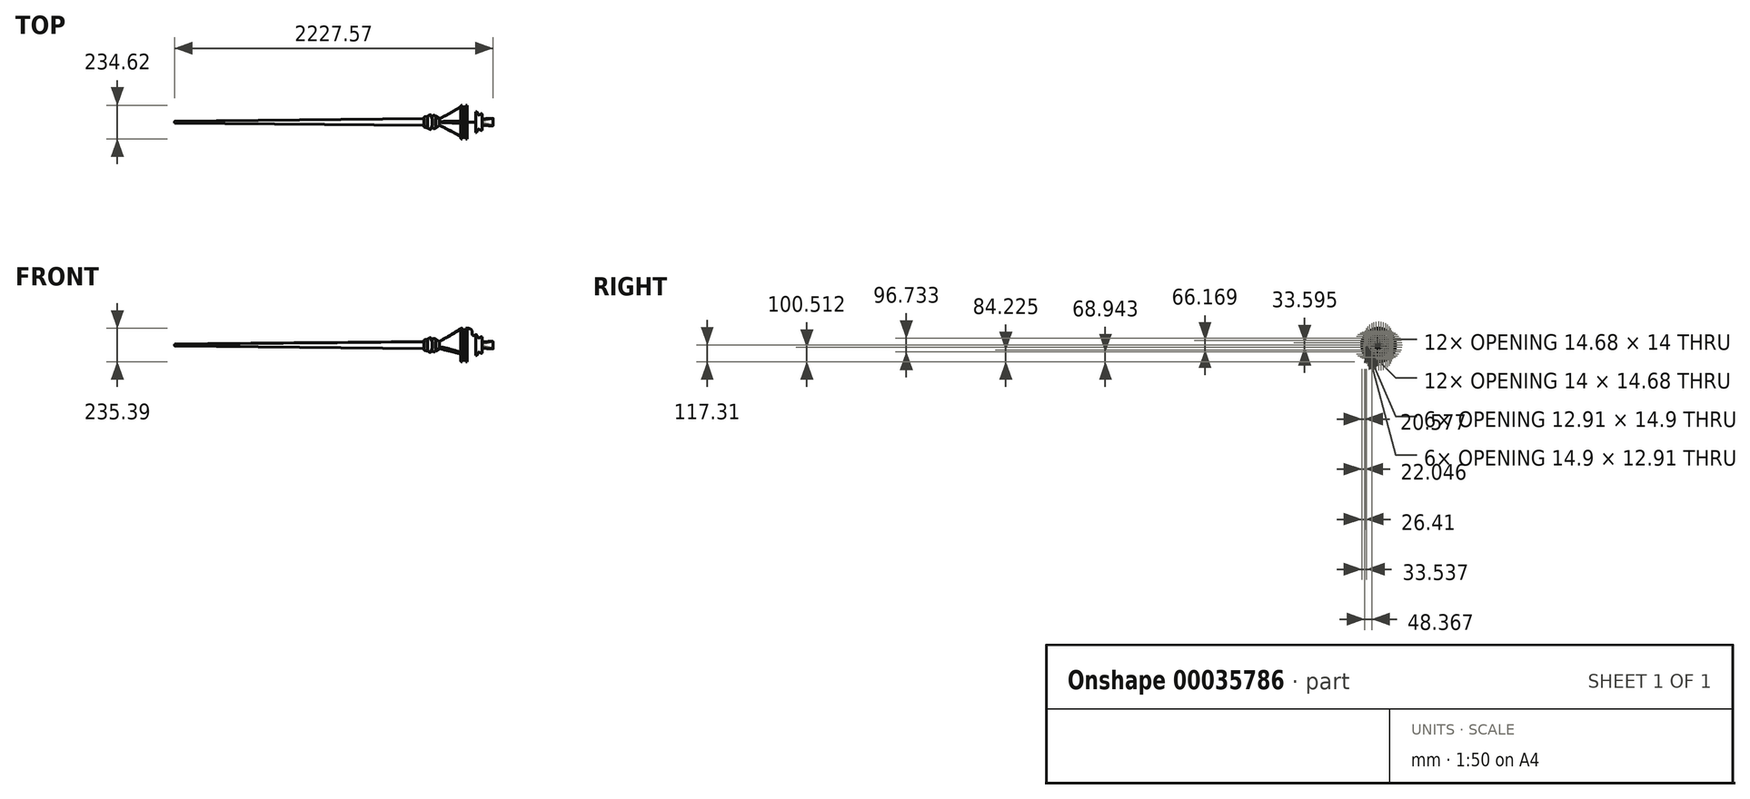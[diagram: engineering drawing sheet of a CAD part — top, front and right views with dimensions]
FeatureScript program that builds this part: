
annotation { "Feature Type Name" : "Feature", "Feature Type Description" : "" }
export const myFeature = defineFeature(function(context is Context, id is Id, definition is map)
    precondition{}
    {
        {
            var Q0;
            Q0=qCreatedBy(makeId("Front.planeOp"),FACE);
            var sketch = newSketch(context, id + "F0", { "sketchPlane" : qUnion([Q0])});
            skLineSegment(sketch, "E0.top", {"start": v(-36.48, 0) * mm, "end": v(43.13, 0) * mm});
            skLineSegment(sketch, "E0.left", {"start": v(-36.48, 5.03) * mm, "end": v(-36.48, 0) * mm});
            skLineSegment(sketch, "E0.right", {"start": v(43.13, 21.56) * mm, "end": v(43.13, 0) * mm});
            skLineSegment(sketch, "E1", {"start": v(-36.48, 5.03) * mm, "end": v(-68.97, 32.77) * mm});
            skLineSegment(sketch, "E2", {"start": v(-68.97, 32.77) * mm, "end": v(-38.76, 38.47) * mm});
            skLineSegment(sketch, "E3", {"start": v(-38.76, 38.47) * mm, "end": v(-17.29, 51.96) * mm});
            skLineSegment(sketch, "E4", {"start": v(-17.29, 51.96) * mm, "end": v(-14.44, 24.41) * mm});
            skLineSegment(sketch, "E5", {"start": v(-14.44, 24.41) * mm, "end": v(-1.7, 21.56) * mm});
            skArc(sketch, "E6", {"start": v(15, 39.61) * mm, "mid": v(-3.59, 40.07) * mm, "end": v(-1.7, 21.56) * mm});
            skLineSegment(sketch, "E7", {"start": v(15, 39.61) * mm, "end": v(43.13, 21.56) * mm});
            skSolve(sketch);
        }
        {
            var Q0;
            Q0=makeQuery(id+"F0.imprint","IMPRINT",FACE,{"disambiguationData":[TD([[makeQuery(id+"F0.imprint","IMPRINT",EDGE,{"derivedFrom":sQuery(id+"F0.wireOp",EDGE,"E0.top")}),1.0]])]});
            var Q1;
            Q1=sQuery(id+"F0.wireOp",EDGE,"E0.top");
            var Q2;
            Q2=sQuery(id+"F0.wireOp",EDGE,"E0.top");
            revolve(context, id + "F1", {"entities" : qUnion([Q0]), "surfaceEntities" : qUnion([Q1]), "axis" : qUnion([Q2]), "revolveType" : RevolveType.FULL});
        }
        {
            var Q0;
            Q0=makeQuery(id+"F1.opRevolve","SWEPT_FACE",FACE,{"disambiguationData":[OSD([sQuery(id+"F0.wireOp",EDGE,"E0.right")])]});
            cPlane(context, id + "F2", {"entities" : qUnion([Q0]), "cplaneType" : CPlaneType.OFFSET, "offset" : 150 * mm, "width" : 150 * mm, "height" : 150 * mm});
        }
        {
            var Q0;
            Q0=qCreatedBy(id+"F2.planeOp",FACE);
            var sketch = newSketch(context, id + "F3", { "sketchPlane" : qUnion([Q0])});
            skCircle(sketch, "E8.cCircle", {"center": v(0, 0) * mm, "radius": 58.56 * mm, "construction": true});
            skLineSegment(sketch, "E8.0", {"start": v(-101.43, -58.56) * mm, "end": v(0, 117.12) * mm});
            skLineSegment(sketch, "E8.1", {"start": v(0, 117.12) * mm, "end": v(101.43, -58.56) * mm});
            skLineSegment(sketch, "E8.2", {"start": v(101.43, -58.56) * mm, "end": v(-101.43, -58.56) * mm});
            skPoint(sketch, "E8.0.midPoint", {"position": v(-50.71, 29.28) * mm});
            skLineSegment(sketch, "E9", {"start": v(0, 0) * mm, "end": v(0, 152.92) * mm, "construction": true});
            skSolve(sketch);
        }
        {
            var Q1;
            Q1=makeQuery(id+"F1.opRevolve","SWEPT_FACE",FACE,{"disambiguationData":[OSD([sQuery(id+"F0.wireOp",EDGE,"E0.right")])]});
            var Q2;
            Q2=makeQuery(id+"F3.imprint","IMPRINT",FACE,{"disambiguationData":[TD([[makeQuery(id+"F3.imprint","IMPRINT",EDGE,{"derivedFrom":sQuery(id+"F3.wireOp",EDGE,"E8.0")}),-1.0]])]});
            loft(context, id + "F4", {"operationType" : NewBodyOperationType.ADD, "sheetProfilesArray" : [{ "sheetProfileEntities" : qUnion([Q1]) }, { "sheetProfileEntities" : qUnion([Q2]) }]});
        }
        {
            var Q0;
            {var subQ0=sQuery(id+"F3.wireOp",EDGE,"E8.2");var subQ1=sQuery(id+"F3.wireOp",EDGE,"E8.1");var subQ2=sQuery(id+"F3.wireOp",EDGE,"E8.0");var subQ3=sQuery(id+"F0.wireOp",EDGE,"E7");var subQ4=sQuery(id+"F0.wireOp",EDGE,"E0.right");Q0=makeQuery(id+"F4.opLoft","SWEPT_EDGE",EDGE,{"disambiguationData":[OSD([subQ4,subQ3,subQ2,subQ1,subQ0]),TDD([makeQuery(id+"F1.opRevolve","SWEPT_EDGE",EDGE,{"disambiguationData":[OSD([subQ4,subQ3])]}),makeQuery(id+"F3.imprint","INTERSECT",VERTEX,{"derivedFrom":[subQ2,subQ1]}),makeQuery(id+"F3.imprint","INTERSECT",VERTEX,{"derivedFrom":[subQ1,subQ0]})])]});}
            var Q1;
            {var subQ0=sQuery(id+"F3.wireOp",EDGE,"E8.2");var subQ1=sQuery(id+"F3.wireOp",EDGE,"E8.1");var subQ2=sQuery(id+"F3.wireOp",EDGE,"E8.0");var subQ3=sQuery(id+"F0.wireOp",EDGE,"E7");var subQ4=sQuery(id+"F0.wireOp",EDGE,"E0.right");Q1=makeQuery(id+"F4.opLoft","SWEPT_EDGE",EDGE,{"disambiguationData":[OSD([subQ4,subQ3,subQ2,subQ1,subQ0]),TDD([makeQuery(id+"F1.opRevolve","SWEPT_EDGE",EDGE,{"disambiguationData":[OSD([subQ4,subQ3])]}),makeQuery(id+"F3.imprint","INTERSECT",VERTEX,{"derivedFrom":[subQ2,subQ0]}),makeQuery(id+"F3.imprint","INTERSECT",VERTEX,{"derivedFrom":[subQ1,subQ0]})])]});}
            var Q2;
            Q2=makeQuery(id+"F4.opLoft","SWEPT_EDGE",EDGE,{"disambiguationData":[OSD([sQuery(id+"F3.wireOp",EDGE,"E8.0"),sQuery(id+"F3.wireOp",EDGE,"E8.2")])]});
            var Q3;
            Q3=makeQuery(id+"F1.opRevolve","SWEPT_EDGE",EDGE,{"disambiguationData":[OSD([sQuery(id+"F0.wireOp",EDGE,"E1"),sQuery(id+"F0.wireOp",EDGE,"E2")])]});
            var Q4;
            Q4=makeQuery(id+"F1.opRevolve","SWEPT_EDGE",EDGE,{"disambiguationData":[OSD([sQuery(id+"F0.wireOp",EDGE,"E3"),sQuery(id+"F0.wireOp",EDGE,"E4")])]});
            var Q5;
            Q5=makeQuery(id+"F1.opRevolve","SWEPT_EDGE",EDGE,{"disambiguationData":[OSD([sQuery(id+"F0.wireOp",EDGE,"E4"),sQuery(id+"F0.wireOp",EDGE,"E5")])]});
            fillet(context, id + "F5", {"entities" : qUnion([Q0, Q1, Q2, Q3, Q4, Q5]), "radius" : 5 * mm, "tangentPropagation" : true, "allowEdgeOverflow" : false});
        }
        {
            var Q0;
            Q0=makeQuery(id+"F4.opLoft","CAP_FACE",FACE,{"disambiguationData":[OSD([makeQuery(id+"F3.imprint","IMPRINT",FACE,{"disambiguationData":[TD([[makeQuery(id+"F3.imprint","IMPRINT",EDGE,{"derivedFrom":sQuery(id+"F3.wireOp",EDGE,"E8.0")}),-1.0]])]})])],"isStart":true});
            cPlane(context, id + "F6", {"entities" : qUnion([Q0]), "cplaneType" : CPlaneType.OFFSET, "offset" : 50 * mm, "width" : 150 * mm, "height" : 150 * mm});
        }
        {
            var Q0;
            Q0=makeQuery(id+"F4.opLoft","CAP_FACE",FACE,{"disambiguationData":[OSD([makeQuery(id+"F3.imprint","IMPRINT",FACE,{"disambiguationData":[TD([[makeQuery(id+"F3.imprint","IMPRINT",EDGE,{"derivedFrom":sQuery(id+"F3.wireOp",EDGE,"E8.0")}),-1.0]])]})])],"isStart":true});
            var Q1;
            Q1=makeQuery(id+"F1.opRevolve","SWEPT_BODY",BODY,{"disambiguationData":[OSD([sQuery(id+"F0.wireOp",EDGE,"E0.top"),sQuery(id+"F0.wireOp",EDGE,"E0.left"),sQuery(id+"F0.wireOp",EDGE,"E0.right"),sQuery(id+"F0.wireOp",EDGE,"E1"),sQuery(id+"F0.wireOp",EDGE,"E2"),sQuery(id+"F0.wireOp",EDGE,"E3"),sQuery(id+"F0.wireOp",EDGE,"E4"),sQuery(id+"F0.wireOp",EDGE,"E5"),sQuery(id+"F0.wireOp",EDGE,"E6"),sQuery(id+"F0.wireOp",EDGE,"E7")])]});
            shell(context, id + "F7", {"entities" : qUnion([Q0]), "parts" : qUnion([Q1]), "thickness" : 2.5 * mm, "oppositeDirection" : true});
        }
        {
            var Q0;
            Q0=makeQuery(id+"F4.opLoft","CAP_FACE",FACE,{"disambiguationData":[OSD([makeQuery(id+"F3.imprint","IMPRINT",FACE,{"disambiguationData":[TD([[makeQuery(id+"F3.imprint","IMPRINT",EDGE,{"derivedFrom":sQuery(id+"F3.wireOp",EDGE,"E8.0")}),-1.0]])]})])],"isStart":true});
            var sketch = newSketch(context, id + "F8", { "sketchPlane" : qUnion([Q0])});
            skCircle(sketch, "E10", {"center": v(0, 0) * mm, "radius": 117.31 * mm});
            skSolve(sketch);
        }
        {
            var Q0;
            Q0 = qSketchRegion(id + "F8", true);
            extrude(context, id + "F9", {"entities" : qUnion([Q0]), "operationType" : NewBodyOperationType.ADD, "depth" : 10 * mm});
        }
        {
            var Q0;
            Q0=makeQuery(id+"F9.opExtrude","CAP_EDGE",EDGE,{"disambiguationData":[OSD([sQuery(id+"F8.wireOp",EDGE,"E10")])],"isStart":true});
            fillet(context, id + "F10", {"entities" : qUnion([Q0]), "radius" : 5 * mm, "tangentPropagation" : true, "allowEdgeOverflow" : false});
        }
        {
            var Q0;
            Q0=makeQuery(id+"F9.opExtrude","CAP_FACE",FACE,{"disambiguationData":[OSD([sQuery(id+"F8.wireOp",EDGE,"E10")])],"isStart":false});
            var sketch = newSketch(context, id + "F11", { "sketchPlane" : qUnion([Q0])});
            skCircle(sketch, "E11.cCircle", {"center": v(96.73, 0) * mm, "radius": 6.45 * mm, "construction": true});
            skLineSegment(sketch, "E11.0", {"start": v(93, 6.45) * mm, "end": v(100.46, 6.45) * mm});
            skLineSegment(sketch, "E11.1", {"start": v(100.46, 6.45) * mm, "end": v(104.19, 0) * mm});
            skLineSegment(sketch, "E11.2", {"start": v(104.19, 0) * mm, "end": v(100.46, -6.45) * mm});
            skLineSegment(sketch, "E11.3", {"start": v(100.46, -6.45) * mm, "end": v(93, -6.45) * mm});
            skLineSegment(sketch, "E11.4", {"start": v(93, -6.45) * mm, "end": v(89.28, 0) * mm});
            skLineSegment(sketch, "E11.5", {"start": v(89.28, 0) * mm, "end": v(93, 6.45) * mm});
            skPoint(sketch, "E11.0.midPoint", {"position": v(96.73, 6.45) * mm});
            skSolve(sketch);
        }
        {
            var Q0;
            Q0 = qSketchRegion(id + "F11", true);
            extrude(context, id + "F12", {"entities" : qUnion([Q0]), "depth" : 25 * mm});
        }
        {
            var Q0;
            Q0=makeQuery(id+"F12.opExtrude","SWEPT_BODY",BODY,{"disambiguationData":[OSD([sQuery(id+"F11.wireOp",EDGE,"E11.0"),sQuery(id+"F11.wireOp",EDGE,"E11.1"),sQuery(id+"F11.wireOp",EDGE,"E11.2"),sQuery(id+"F11.wireOp",EDGE,"E11.3"),sQuery(id+"F11.wireOp",EDGE,"E11.4"),sQuery(id+"F11.wireOp",EDGE,"E11.5")])]});
            var Q1;
            Q1=sQuery(id+"F0.wireOp",EDGE,"E0.top");
            circularPattern(context, id + "F13", {"operationType" : NewBodyOperationType.ADD, "entities" : qUnion([Q0]), "axis" : qUnion([Q1]), "angle" : 360 * degree, "instanceCount" : 36, "equalSpace" : true});
        }
        {
            var Q0;
            Q0=makeQuery(id+"F13.opPattern","COPY",FACE,{"derivedFrom":makeQuery(id+"F12.opExtrude","CAP_FACE",FACE,{"disambiguationData":[OSD([sQuery(id+"F11.wireOp",EDGE,"E11.0"),sQuery(id+"F11.wireOp",EDGE,"E11.1"),sQuery(id+"F11.wireOp",EDGE,"E11.2"),sQuery(id+"F11.wireOp",EDGE,"E11.3"),sQuery(id+"F11.wireOp",EDGE,"E11.4"),sQuery(id+"F11.wireOp",EDGE,"E11.5")])],"isStart":false}),"instanceName":"5"});
            var sketch = newSketch(context, id + "F14", { "sketchPlane" : qUnion([Q0])});
            skCircle(sketch, "E12.0", {"center": v(0, 0) * mm, "radius": 117.31 * mm});
            skSolve(sketch);
        }
        {
            var Q0;
            Q0 = qSketchRegion(id + "F14", true);
            extrude(context, id + "F15", {"entities" : qUnion([Q0]), "operationType" : NewBodyOperationType.ADD, "depth" : 10 * mm});
        }
        {
            var Q0;
            Q0=qCreatedBy(makeId("Front.planeOp"),FACE);
            var sketch = newSketch(context, id + "F16", { "sketchPlane" : qUnion([Q0])});
            skLineSegment(sketch, "E13.0", {"start": v(238.13, 117.31) * mm, "end": v(238.13, 0) * mm});
            skLineSegment(sketch, "E14", {"start": v(238.13, 0) * mm, "end": v(308, 0) * mm});
            skPoint(sketch, "E14.endSnap0", {"position": v(238.13, 0) * mm});
            skPoint(sketch, "E15.orphan", {"position": v(238.13, -117.31) * mm});
            skLineSegment(sketch, "E16", {"start": v(341.4, 20.36) * mm, "end": v(341.4, 61.37) * mm});
            skLineSegment(sketch, "E17", {"start": v(341.4, 61.37) * mm, "end": v(319.15, 50.24) * mm});
            skLineSegment(sketch, "E18", {"start": v(312.43, 52.5) * mm, "end": v(303.9, 69.77) * mm});
            skFitSpline(sketch, "E19", {"points": [v(301.58, 74.44) * mm, v(238.13, 117.31) * mm], "startDerivative": vector(-179.2, -101.63) * mm, "endDerivative": vector(-197.49, 0.23) * mm});
            skArc(sketch, "E20.filletArc", {"start": v(303.9, 69.77) * mm, "mid": v(300.95, 72.3) * mm, "end": v(297.08, 71.98) * mm});
            skPoint(sketch, "E21.visualSharp", {"position": v(314.66, 48) * mm});
            skArc(sketch, "E21.filletArc", {"start": v(312.43, 52.5) * mm, "mid": v(315.32, 49.97) * mm, "end": v(319.15, 50.24) * mm});
            skPoint(sketch, "E22.visualSharp", {"position": v(341.4, 19.4) * mm});
            skFitSpline(sketch, "E23", {"points": [v(341.4, 20.36) * mm, v(308, 0) * mm], "startDerivative": vector(430.58, 46.21) * mm, "endDerivative": vector(-281.28, -49.2) * mm});
            skFitSpline(sketch, "E24", {"points": [v(405.05, 25.86) * mm, v(447.74, 37.3) * mm, v(467.32, 27.84) * mm, v(407.34, 20.2) * mm], "startDerivative": vector(127.23, 68.44) * mm, "endDerivative": vector(-224.16, 32.5) * mm});
            skSolve(sketch);
        }
        {
            var Q0;
            Q0=makeQuery(id+"F16.imprint","IMPRINT",FACE,{"disambiguationData":[TD([[makeQuery(id+"F16.imprint","IMPRINT",EDGE,{"derivedFrom":sQuery(id+"F16.wireOp",EDGE,"E13.0")}),1.0]])]});
            var Q1;
            Q1=sQuery(id+"F16.wireOp",EDGE,"E14");
            revolve(context, id + "F17", {"operationType" : NewBodyOperationType.ADD, "entities" : qUnion([Q0]), "axis" : qUnion([Q1]), "revolveType" : RevolveType.FULL});
        }
        {
            var Q0;
            Q0=makeQuery(id+"F17.opRevolve","SWEPT_EDGE",EDGE,{"disambiguationData":[OSD([sQuery(id+"F16.wireOp",EDGE,"E16"),sQuery(id+"F16.wireOp",EDGE,"E17")])]});
            var Q1;
            Q1=makeQuery(id+"F17.opRevolve","SWEPT_EDGE",EDGE,{"disambiguationData":[OSD([sQuery(id+"F16.wireOp",EDGE,"E16"),sQuery(id+"F16.wireOp",EDGE,"E23")])]});
            fillet(context, id + "F18", {"entities" : qUnion([Q0, Q1]), "radius" : 5 * mm, "tangentPropagation" : true, "allowEdgeOverflow" : false});
        }
        {
            var Q0;
            {var subQ9=sQuery(id+"F8.wireOp",EDGE,"E10");Q0=makeQuery(id+"F10.opFillet","SPLIT",FACE,{"disambiguationData":[OD(0.0)],"derivedFrom":makeQuery(id+"F9.boolean.opBoolean","SPLIT",FACE,{"disambiguationData":[TD([makeQuery(id+"F9.opExtrude","SWEPT_FACE",FACE,{"disambiguationData":[OSD([subQ9])]})])],"derivedFrom":makeQuery(id+"F9.opExtrude","CAP_FACE",FACE,{"disambiguationData":[OSD([subQ9])],"isStart":true})})});}
            cPlane(context, id + "F19", {"entities" : qUnion([Q0]), "cplaneType" : CPlaneType.OFFSET, "offset" : 252 * mm, "width" : 150 * mm, "height" : 150 * mm});
        }
        {
            var Q0;
            Q0=qCreatedBy(id+"F19.planeOp",FACE);
            var sketch = newSketch(context, id + "F20", { "sketchPlane" : qUnion([Q0])});
            skCircle(sketch, "E25.0", {"center": v(0, 0) * mm, "radius": 24.1 * mm});
            skSolve(sketch);
        }
        {
            var Q0;
            Q0=makeQuery(id+"F20.imprint","IMPRINT",FACE,{"disambiguationData":[TD([[makeQuery(id+"F20.imprint","IMPRINT",EDGE,{"derivedFrom":sQuery(id+"F20.wireOp",EDGE,"E25.0")}),1.0]])]});
            cPlane(context, id + "F21", {"entities" : qUnion([Q0]), "cplaneType" : CPlaneType.OFFSET, "offset" : 1750 * mm, "width" : 150 * mm, "height" : 150 * mm});
        }
        {
            var Q0;
            Q0=qCreatedBy(id+"F21.planeOp",FACE);
            var sketch = newSketch(context, id + "F22", { "sketchPlane" : qUnion([Q0])});
            skCircle(sketch, "E26", {"center": v(0, 0) * mm, "radius": 6.58 * mm});
            skSolve(sketch);
        }
        {
            var Q1;
            Q1 = qSketchRegion(id + "F20", true);
            var Q2;
            Q2 = qSketchRegion(id + "F22", true);
            loft(context, id + "F23", {"operationType" : NewBodyOperationType.ADD, "sheetProfilesArray" : [{ "sheetProfileEntities" : qUnion([Q1]) }, { "sheetProfileEntities" : qUnion([Q2]) }]});
        }
        {
            var Q0;
            Q0=makeQuery(id+"F23.opLoft","MID_CAP_EDGE",EDGE,{"disambiguationData":[OSD([sQuery(id+"F20.wireOp",EDGE,"E25.0"),sQuery(id+"F22.wireOp",EDGE,"E26")])],"capPos":1.0});
            fillet(context, id + "F24", {"entities" : qUnion([Q0]), "radius" : 5 * mm, "tangentPropagation" : true, "allowEdgeOverflow" : false});
        }
    });
